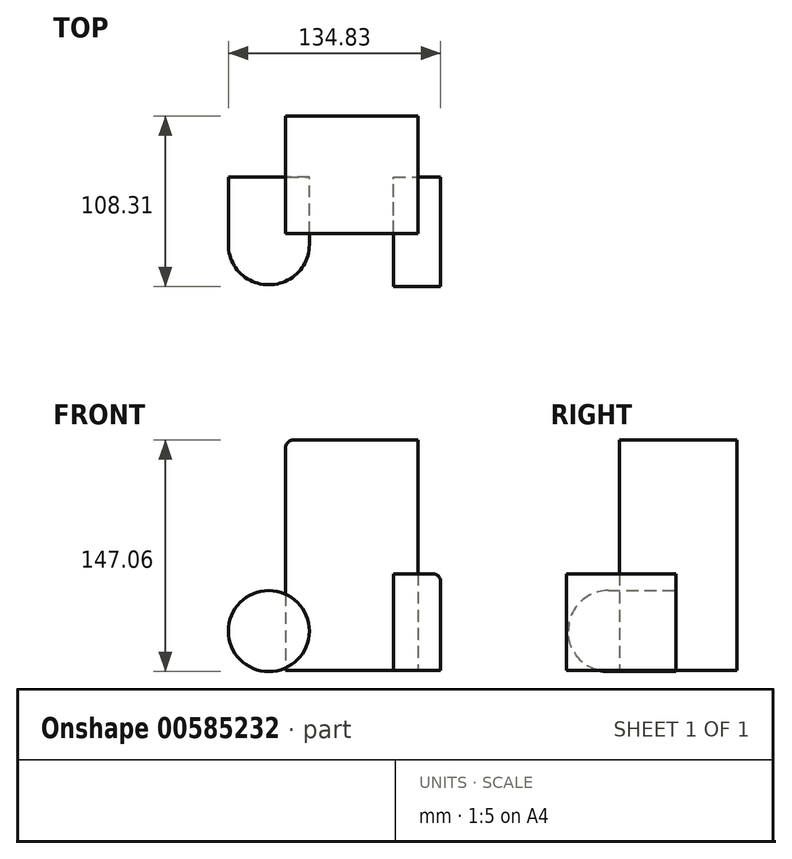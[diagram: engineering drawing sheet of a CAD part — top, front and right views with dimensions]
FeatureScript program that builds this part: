
annotation { "Feature Type Name" : "Feature", "Feature Type Description" : "" }
export const myFeature = defineFeature(function(context is Context, id is Id, definition is map)
    precondition{}
    {
        {
            var Q0;
            Q0=qCreatedBy(makeId("Front.planeOp"),FACE);
            var sketch = newSketch(context, id + "F0", { "sketchPlane" : qUnion([Q0])});
            skLineSegment(sketch, "E0.bottom", {"start": v(29.05, 0) * mm, "end": v(58.88, 0) * mm});
            skLineSegment(sketch, "E0.top", {"start": v(29.05, 61.3) * mm, "end": v(58.88, 61.3) * mm});
            skLineSegment(sketch, "E0.left", {"start": v(29.05, 0) * mm, "end": v(29.05, 61.3) * mm});
            skLineSegment(sketch, "E0.right", {"start": v(58.88, 0) * mm, "end": v(58.88, 61.3) * mm});
            skSolve(sketch);
        }
        {
            var Q0;
            Q0 = qSketchRegion(id + "F0", true);
            extrude(context, id + "F1", {"entities" : qUnion([Q0]), "depth" : 69.44 * mm, "offsetDistance" : 25.4 * mm});
        }
        {
            var Q0;
            Q0=makeQuery(id+"F1.opExtrude","SWEPT_EDGE",EDGE,{"disambiguationData":[OSD([sQuery(id+"F0.wireOp",EDGE,"E0.top"),sQuery(id+"F0.wireOp",EDGE,"E0.right")])]});
            fillet(context, id + "F2", {"entities" : qUnion([Q0]), "radius" : 5.08 * mm, "tangentPropagation" : true, "allowEdgeOverflow" : false});
        }
        {
            var Q0;
            Q0=qCreatedBy(makeId("Front.planeOp"),FACE);
            var sketch = newSketch(context, id + "F3", { "sketchPlane" : qUnion([Q0])});
            skCircle(sketch, "E1", {"center": v(-50.23, 24.87) * mm, "radius": 25.71 * mm});
            skSolve(sketch);
        }
        {
            var Q0;
            Q0 = qSketchRegion(id + "F3", true);
            extrude(context, id + "F4", {"entities" : qUnion([Q0]), "depth" : 68.3 * mm, "offsetDistance" : 25.4 * mm});
        }
        {
            var Q0;
            Q0=makeQuery(id+"F4.opExtrude","CAP_EDGE",EDGE,{"disambiguationData":[OSD([sQuery(id+"F3.wireOp",EDGE,"E1")])],"isStart":false});
            fillet(context, id + "F5", {"entities" : qUnion([Q0]), "radius" : 25.4 * mm, "tangentPropagation" : true, "allowEdgeOverflow" : false});
        }
        {
            var Q0;
            Q0=qCreatedBy(makeId("Top.planeOp"),FACE);
            var sketch = newSketch(context, id + "F6", { "sketchPlane" : qUnion([Q0])});
            skLineSegment(sketch, "E2.bottom", {"start": v(-39.6, 38.87) * mm, "end": v(44.54, 38.87) * mm});
            skLineSegment(sketch, "E2.top", {"start": v(-39.6, -35.75) * mm, "end": v(44.54, -35.75) * mm});
            skLineSegment(sketch, "E2.left", {"start": v(-39.6, 38.87) * mm, "end": v(-39.6, -35.75) * mm});
            skLineSegment(sketch, "E2.right", {"start": v(44.54, 38.87) * mm, "end": v(44.54, -35.75) * mm});
            skSolve(sketch);
        }
        {
            var Q0;
            Q0 = qSketchRegion(id + "F6", true);
            extrude(context, id + "F7", {"entities" : qUnion([Q0]), "depth" : 146.22 * mm, "offsetDistance" : 25.4 * mm});
        }
        {
            var Q0;
            Q0=makeQuery(id+"F7.opExtrude","CAP_EDGE",EDGE,{"disambiguationData":[OSD([sQuery(id+"F6.wireOp",EDGE,"E2.left")])],"isStart":false});
            fillet(context, id + "F8", {"entities" : qUnion([Q0]), "radius" : 5.08 * mm, "tangentPropagation" : true, "allowEdgeOverflow" : false});
        }
    });
